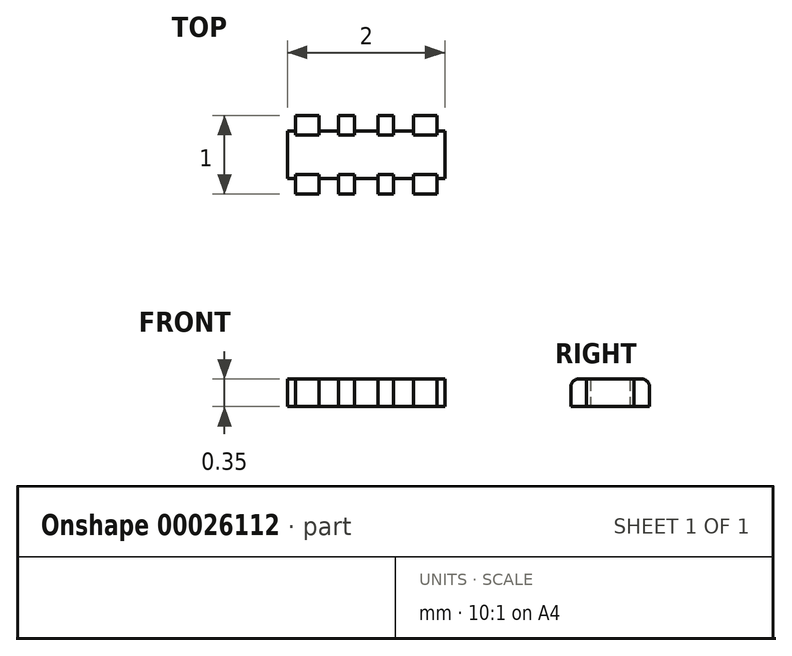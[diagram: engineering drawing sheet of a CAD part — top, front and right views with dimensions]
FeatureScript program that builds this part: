
annotation { "Feature Type Name" : "Feature", "Feature Type Description" : "" }
export const myFeature = defineFeature(function(context is Context, id is Id, definition is map)
    precondition{}
    {
        {
            var Q0;
            Q0=qCreatedBy(makeId("Top.planeOp"),FACE);
            var sketch = newSketch(context, id + "F0", { "sketchPlane" : qUnion([Q0])});
            skLineSegment(sketch, "E0.rect.bottom", {"start": v(1, -0.3) * mm, "end": v(-1, -0.3) * mm});
            skLineSegment(sketch, "E0.rect.top", {"start": v(1, 0.3) * mm, "end": v(-1, 0.3) * mm});
            skLineSegment(sketch, "E0.rect.left", {"start": v(1, -0.3) * mm, "end": v(1, 0.3) * mm});
            skLineSegment(sketch, "E0.rect.right", {"start": v(-1, -0.3) * mm, "end": v(-1, 0.3) * mm});
            skPoint(sketch, "E0.rect.middle", {"position": v(0, 0) * mm});
            skSolve(sketch);
        }
        {
            var Q0;
            Q0=makeQuery(id+"F0.imprint","IMPRINT",FACE,{"disambiguationData":[TD([[makeQuery(id+"F0.imprint","IMPRINT",EDGE,{"derivedFrom":sQuery(id+"F0.wireOp",EDGE,"E0.rect.bottom")}),-1.0]])]});
            extrude(context, id + "F1", {"entities" : qUnion([Q0]), "depth" : 0.35 * mm});
        }
        {
            var Q0;
            Q0=qCreatedBy(makeId("Top.planeOp"),FACE);
            var sketch = newSketch(context, id + "F2", { "sketchPlane" : qUnion([Q0])});
            skLineSegment(sketch, "E1.rect.bottom", {"start": v(-0.6, -0.5) * mm, "end": v(-0.9, -0.5) * mm});
            skLineSegment(sketch, "E1.rect.top", {"start": v(-0.6, -0.25) * mm, "end": v(-0.9, -0.25) * mm});
            skLineSegment(sketch, "E1.rect.left", {"start": v(-0.6, -0.5) * mm, "end": v(-0.6, -0.25) * mm});
            skLineSegment(sketch, "E1.rect.right", {"start": v(-0.9, -0.5) * mm, "end": v(-0.9, -0.25) * mm});
            skPoint(sketch, "E1.rect.middle", {"position": v(-0.75, -0.38) * mm});
            skLineSegment(sketch, "E2.MirrorCS", {"start": v(0.9, -0.5) * mm, "end": v(0.9, -0.25) * mm});
            skLineSegment(sketch, "E3.MirrorCS", {"start": v(0.6, -0.25) * mm, "end": v(0.9, -0.25) * mm});
            skLineSegment(sketch, "E4.MirrorCS", {"start": v(0.6, -0.5) * mm, "end": v(0.9, -0.5) * mm});
            skLineSegment(sketch, "E5.MirrorCS", {"start": v(0.6, -0.5) * mm, "end": v(0.6, -0.25) * mm});
            skLineSegment(sketch, "E6.MirrorCS", {"start": v(0.6, 0.25) * mm, "end": v(0.9, 0.25) * mm});
            skLineSegment(sketch, "E7.MirrorCS", {"start": v(0.6, 0.5) * mm, "end": v(0.6, 0.25) * mm});
            skLineSegment(sketch, "E8.MirrorCS", {"start": v(0.9, 0.5) * mm, "end": v(0.9, 0.25) * mm});
            skLineSegment(sketch, "E9.MirrorCS", {"start": v(0.6, 0.5) * mm, "end": v(0.9, 0.5) * mm});
            skLineSegment(sketch, "E10.MirrorCS", {"start": v(-0.9, 0.5) * mm, "end": v(-0.9, 0.25) * mm});
            skLineSegment(sketch, "E11.MirrorCS", {"start": v(-0.6, 0.25) * mm, "end": v(-0.9, 0.25) * mm});
            skLineSegment(sketch, "E12.MirrorCS", {"start": v(-0.6, 0.5) * mm, "end": v(-0.6, 0.25) * mm});
            skLineSegment(sketch, "E13.MirrorCS", {"start": v(-0.6, 0.5) * mm, "end": v(-0.9, 0.5) * mm});
            skLineSegment(sketch, "E14.rect.bottom", {"start": v(-0.15, 0.25) * mm, "end": v(-0.35, 0.25) * mm});
            skLineSegment(sketch, "E14.rect.top", {"start": v(-0.15, 0.5) * mm, "end": v(-0.35, 0.5) * mm});
            skLineSegment(sketch, "E14.rect.left", {"start": v(-0.15, 0.25) * mm, "end": v(-0.15, 0.5) * mm});
            skLineSegment(sketch, "E14.rect.right", {"start": v(-0.35, 0.25) * mm, "end": v(-0.35, 0.5) * mm});
            skPoint(sketch, "E14.rect.middle", {"position": v(-0.25, 0.38) * mm});
            skLineSegment(sketch, "E15.MirrorCS", {"start": v(0.15, 0.25) * mm, "end": v(0.15, 0.5) * mm});
            skLineSegment(sketch, "E16.MirrorCS", {"start": v(0.15, 0.5) * mm, "end": v(0.35, 0.5) * mm});
            skLineSegment(sketch, "E17.MirrorCS", {"start": v(0.35, 0.25) * mm, "end": v(0.35, 0.5) * mm});
            skLineSegment(sketch, "E18.MirrorCS", {"start": v(0.15, 0.25) * mm, "end": v(0.35, 0.25) * mm});
            skLineSegment(sketch, "E19.MirrorCS", {"start": v(-0.35, -0.25) * mm, "end": v(-0.35, -0.5) * mm});
            skLineSegment(sketch, "E20.MirrorCS", {"start": v(-0.15, -0.25) * mm, "end": v(-0.35, -0.25) * mm});
            skLineSegment(sketch, "E21.MirrorCS", {"start": v(-0.15, -0.25) * mm, "end": v(-0.15, -0.5) * mm});
            skLineSegment(sketch, "E22.MirrorCS", {"start": v(-0.15, -0.5) * mm, "end": v(-0.35, -0.5) * mm});
            skLineSegment(sketch, "E23.MirrorCS", {"start": v(0.15, -0.5) * mm, "end": v(0.35, -0.5) * mm});
            skLineSegment(sketch, "E24.MirrorCS", {"start": v(0.15, -0.25) * mm, "end": v(0.15, -0.5) * mm});
            skLineSegment(sketch, "E25.MirrorCS", {"start": v(0.15, -0.25) * mm, "end": v(0.35, -0.25) * mm});
            skLineSegment(sketch, "E26.MirrorCS", {"start": v(0.35, -0.25) * mm, "end": v(0.35, -0.5) * mm});
            skSolve(sketch);
        }
        {
            var Q0;
            Q0=qSketchRegion(id+"F2",true);
            extrude(context, id + "F3", {"entities" : qUnion([Q0]), "depth" : 0.35 * mm});
        }
        {
            var Q0;
            Q0=makeQuery(id+"F3.opExtrude","CAP_EDGE",EDGE,{"disambiguationData":[OSD([sQuery(id+"F2.wireOp",EDGE,"E9.MirrorCS")])],"isStart":false});
            var Q1;
            Q1=makeQuery(id+"F3.opExtrude","CAP_EDGE",EDGE,{"disambiguationData":[OSD([sQuery(id+"F2.wireOp",EDGE,"E16.MirrorCS")])],"isStart":false});
            var Q2;
            Q2=makeQuery(id+"F3.opExtrude","CAP_EDGE",EDGE,{"disambiguationData":[OSD([sQuery(id+"F2.wireOp",EDGE,"E14.rect.top")])],"isStart":false});
            var Q3;
            Q3=makeQuery(id+"F3.opExtrude","CAP_EDGE",EDGE,{"disambiguationData":[OSD([sQuery(id+"F2.wireOp",EDGE,"E13.MirrorCS")])],"isStart":false});
            var Q4;
            Q4=makeQuery(id+"F3.opExtrude","CAP_EDGE",EDGE,{"disambiguationData":[OSD([sQuery(id+"F2.wireOp",EDGE,"E4.MirrorCS")])],"isStart":false});
            var Q5;
            Q5=makeQuery(id+"F3.opExtrude","CAP_EDGE",EDGE,{"disambiguationData":[OSD([sQuery(id+"F2.wireOp",EDGE,"E23.MirrorCS")])],"isStart":false});
            var Q6;
            Q6=makeQuery(id+"F3.opExtrude","CAP_EDGE",EDGE,{"disambiguationData":[OSD([sQuery(id+"F2.wireOp",EDGE,"E22.MirrorCS")])],"isStart":false});
            var Q7;
            Q7=makeQuery(id+"F3.opExtrude","CAP_EDGE",EDGE,{"disambiguationData":[OSD([sQuery(id+"F2.wireOp",EDGE,"E1.rect.bottom")])],"isStart":false});
            fillet(context, id + "F4", {"entities" : qUnion([Q0, Q1, Q2, Q3, Q4, Q5, Q6, Q7]), "radius" : 0.1 * mm, "tangentPropagation" : true, "allowEdgeOverflow" : false});
        }
        {
            var Q0;
            Q0=makeQuery(id+"F3.opExtrude","SWEPT_BODY",BODY,{"disambiguationData":[OSD([sQuery(id+"F2.wireOp",EDGE,"E1.rect.bottom"),sQuery(id+"F2.wireOp",EDGE,"E1.rect.top"),sQuery(id+"F2.wireOp",EDGE,"E1.rect.left"),sQuery(id+"F2.wireOp",EDGE,"E1.rect.right")])]});
            var Q1;
            Q1=makeQuery(id+"F1.opExtrude","SWEPT_BODY",BODY,{"disambiguationData":[OSD([sQuery(id+"F0.wireOp",EDGE,"E0.rect.bottom"),sQuery(id+"F0.wireOp",EDGE,"E0.rect.top"),sQuery(id+"F0.wireOp",EDGE,"E0.rect.left"),sQuery(id+"F0.wireOp",EDGE,"E0.rect.right")])]});
            booleanBodies(context, id + "F5", {"operationType" : BooleanOperationType.SUBTRACTION, "tools" : qUnion([Q0]), "targets" : qUnion([Q1]), "keepTools" : true});
        }
        {
            var Q0;
            Q0=makeQuery(id+"F3.opExtrude","SWEPT_BODY",BODY,{"disambiguationData":[OSD([sQuery(id+"F2.wireOp",EDGE,"E2.MirrorCS"),sQuery(id+"F2.wireOp",EDGE,"E3.MirrorCS"),sQuery(id+"F2.wireOp",EDGE,"E4.MirrorCS"),sQuery(id+"F2.wireOp",EDGE,"E5.MirrorCS")])]});
            var Q1;
            Q1=makeQuery(id+"F3.opExtrude","SWEPT_BODY",BODY,{"disambiguationData":[OSD([sQuery(id+"F2.wireOp",EDGE,"E6.MirrorCS"),sQuery(id+"F2.wireOp",EDGE,"E7.MirrorCS"),sQuery(id+"F2.wireOp",EDGE,"E8.MirrorCS"),sQuery(id+"F2.wireOp",EDGE,"E9.MirrorCS")])]});
            var Q2;
            Q2=makeQuery(id+"F3.opExtrude","SWEPT_BODY",BODY,{"disambiguationData":[OSD([sQuery(id+"F2.wireOp",EDGE,"E10.MirrorCS"),sQuery(id+"F2.wireOp",EDGE,"E11.MirrorCS"),sQuery(id+"F2.wireOp",EDGE,"E12.MirrorCS"),sQuery(id+"F2.wireOp",EDGE,"E13.MirrorCS")])]});
            var Q3;
            Q3=makeQuery(id+"F3.opExtrude","SWEPT_BODY",BODY,{"disambiguationData":[OSD([sQuery(id+"F2.wireOp",EDGE,"E14.rect.bottom"),sQuery(id+"F2.wireOp",EDGE,"E14.rect.top"),sQuery(id+"F2.wireOp",EDGE,"E14.rect.left"),sQuery(id+"F2.wireOp",EDGE,"E14.rect.right")])]});
            var Q4;
            Q4=makeQuery(id+"F3.opExtrude","SWEPT_BODY",BODY,{"disambiguationData":[OSD([sQuery(id+"F2.wireOp",EDGE,"E15.MirrorCS"),sQuery(id+"F2.wireOp",EDGE,"E16.MirrorCS"),sQuery(id+"F2.wireOp",EDGE,"E17.MirrorCS"),sQuery(id+"F2.wireOp",EDGE,"E18.MirrorCS")])]});
            var Q5;
            Q5=makeQuery(id+"F3.opExtrude","SWEPT_BODY",BODY,{"disambiguationData":[OSD([sQuery(id+"F2.wireOp",EDGE,"E19.MirrorCS"),sQuery(id+"F2.wireOp",EDGE,"E20.MirrorCS"),sQuery(id+"F2.wireOp",EDGE,"E21.MirrorCS"),sQuery(id+"F2.wireOp",EDGE,"E22.MirrorCS")])]});
            var Q6;
            Q6=makeQuery(id+"F3.opExtrude","SWEPT_BODY",BODY,{"disambiguationData":[OSD([sQuery(id+"F2.wireOp",EDGE,"E23.MirrorCS"),sQuery(id+"F2.wireOp",EDGE,"E24.MirrorCS"),sQuery(id+"F2.wireOp",EDGE,"E25.MirrorCS"),sQuery(id+"F2.wireOp",EDGE,"E26.MirrorCS")])]});
            var Q7;
            Q7=makeQuery(id+"F1.opExtrude","SWEPT_BODY",BODY,{"disambiguationData":[OSD([sQuery(id+"F0.wireOp",EDGE,"E0.rect.bottom"),sQuery(id+"F0.wireOp",EDGE,"E0.rect.top"),sQuery(id+"F0.wireOp",EDGE,"E0.rect.left"),sQuery(id+"F0.wireOp",EDGE,"E0.rect.right")])]});
            booleanBodies(context, id + "F6", {"operationType" : BooleanOperationType.SUBTRACTION, "tools" : qUnion([Q0, Q1, Q2, Q3, Q4, Q5, Q6]), "targets" : qUnion([Q7]), "keepTools" : true});
        }
    });
